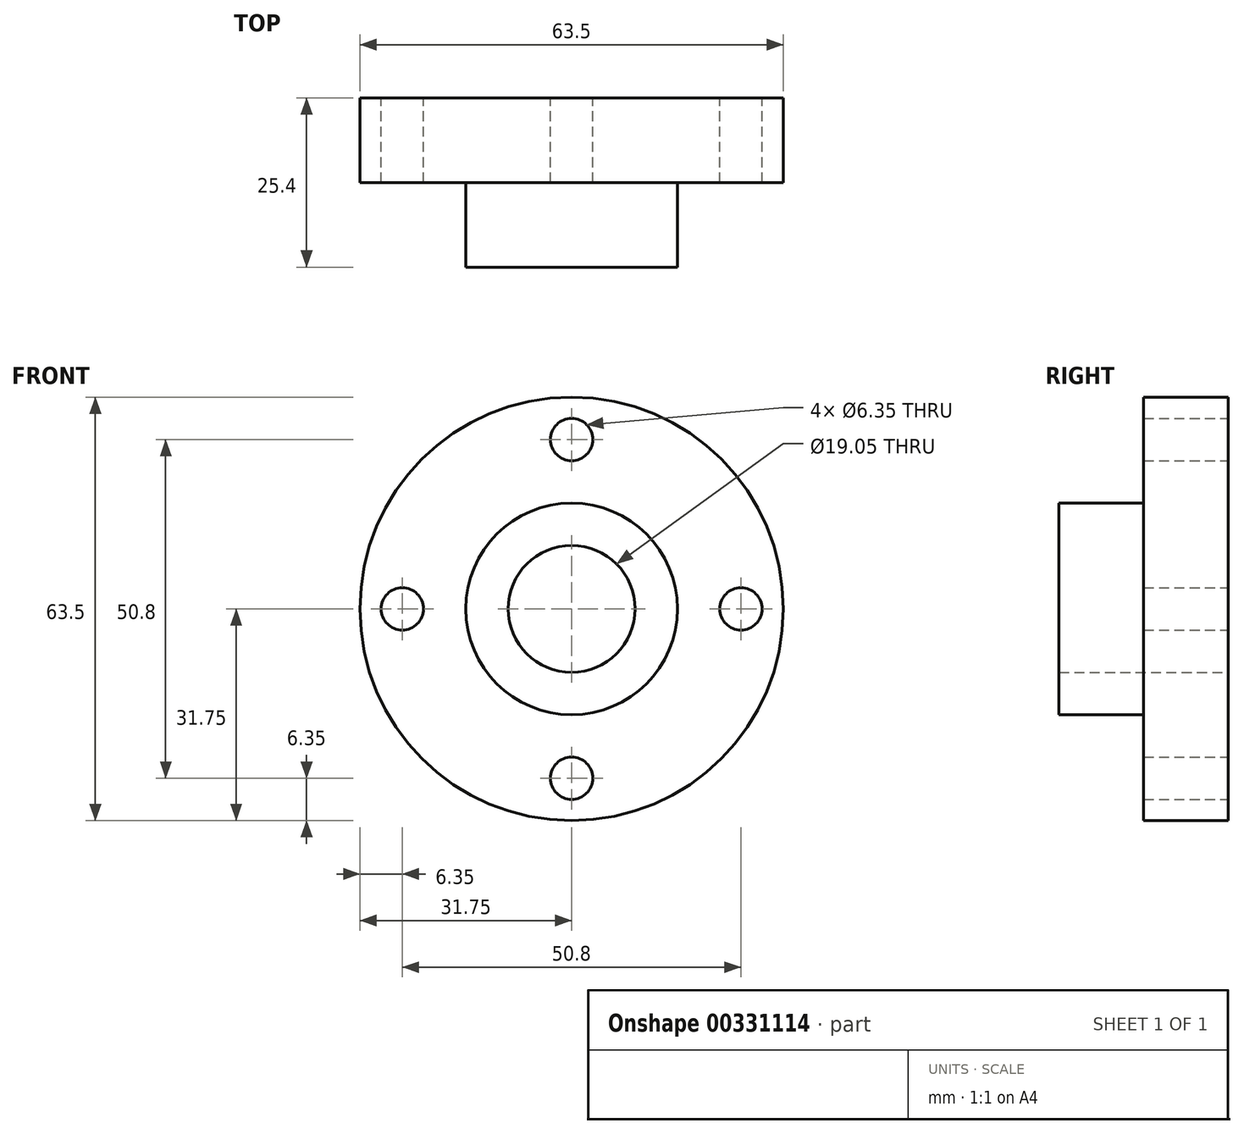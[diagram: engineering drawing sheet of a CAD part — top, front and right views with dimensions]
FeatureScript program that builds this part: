
annotation { "Feature Type Name" : "Feature", "Feature Type Description" : "" }
export const myFeature = defineFeature(function(context is Context, id is Id, definition is map)
    precondition{}
    {
        {
            var Q0;
            Q0=qCreatedBy(makeId("Front.planeOp"),FACE);
            var sketch = newSketch(context, id + "F0", { "sketchPlane" : qUnion([Q0])});
            skCircle(sketch, "E0", {"center": v(0, 0) * mm, "radius": 31.75 * mm});
            skCircle(sketch, "E1", {"center": v(0, 0) * mm, "radius": 25.4 * mm, "construction": true});
            skCircle(sketch, "E2", {"center": v(0, 0) * mm, "radius": 15.88 * mm});
            skCircle(sketch, "E3", {"center": v(0, 0) * mm, "radius": 9.53 * mm});
            skCircle(sketch, "E4", {"center": v(-25.4, 0) * mm, "radius": 3.18 * mm});
            skCircle(sketch, "E5", {"center": v(25.4, 0) * mm, "radius": 3.18 * mm});
            skCircle(sketch, "E6", {"center": v(0, -25.4) * mm, "radius": 3.18 * mm});
            skCircle(sketch, "E7", {"center": v(0, 25.4) * mm, "radius": 3.18 * mm});
            skSolve(sketch);
        }
        {
            var Q0;
            Q0=makeQuery(id+"F0.imprint","IMPRINT",FACE,{"disambiguationData":[TD([[makeQuery(id+"F0.imprint","IMPRINT",EDGE,{"derivedFrom":sQuery(id+"F0.wireOp",EDGE,"E0")}),1.0]])]});
            extrude(context, id + "F1", {"entities" : qUnion([Q0]), "depth" : 12.7 * mm});
        }
        {
            var Q0;
            Q0=makeQuery(id+"F0.imprint","IMPRINT",FACE,{"disambiguationData":[TD([[makeQuery(id+"F0.imprint","IMPRINT",EDGE,{"derivedFrom":sQuery(id+"F0.wireOp",EDGE,"E2")}),1.0]])]});
            extrude(context, id + "F2", {"entities" : qUnion([Q0]), "operationType" : NewBodyOperationType.ADD, "depth" : 25.4 * mm});
        }
    });
